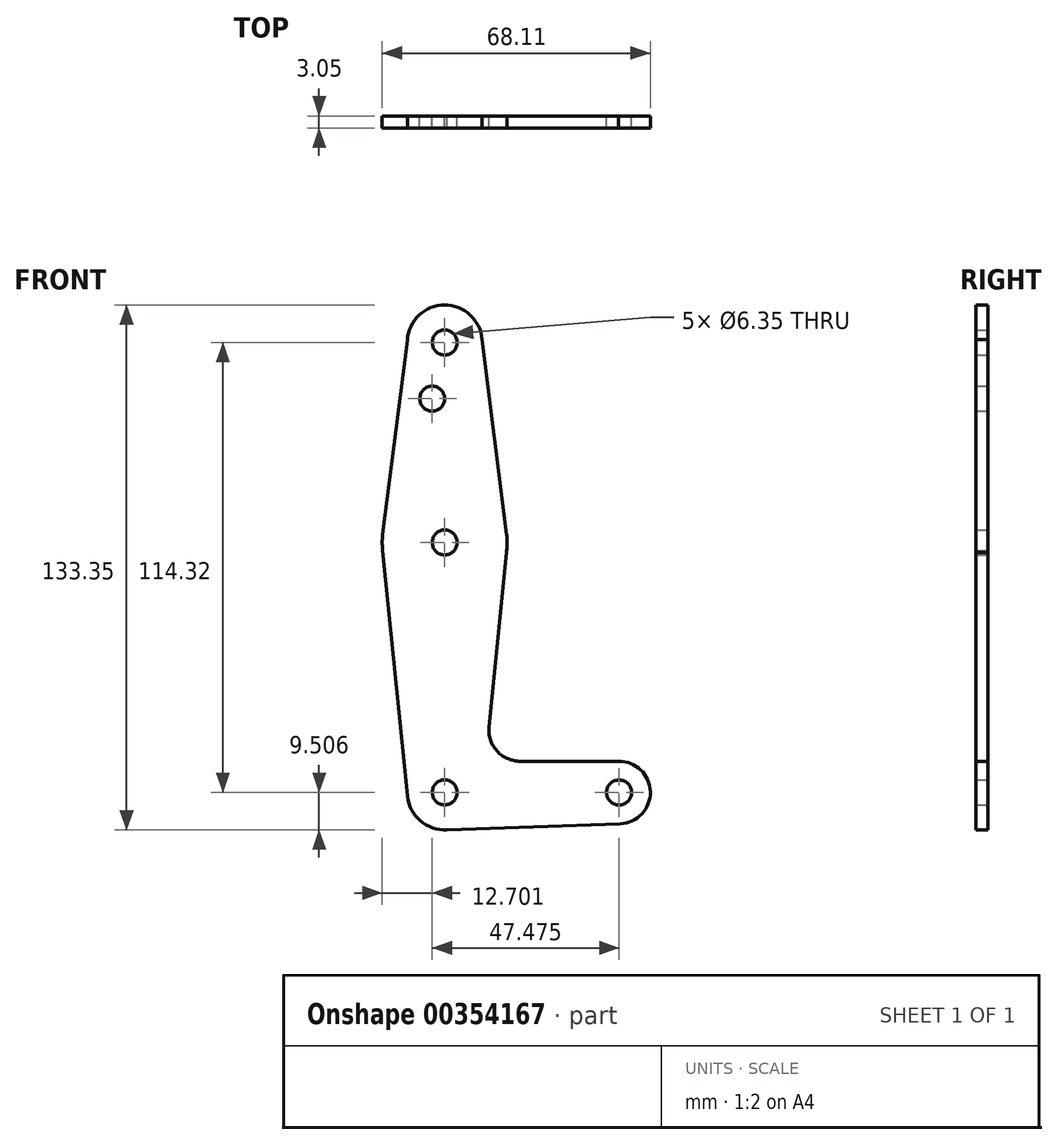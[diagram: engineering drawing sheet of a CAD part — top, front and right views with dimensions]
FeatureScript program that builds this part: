
annotation { "Feature Type Name" : "Feature", "Feature Type Description" : "" }
export const myFeature = defineFeature(function(context is Context, id is Id, definition is map)
    precondition{}
    {
        {
            var Q0;
            Q0=qCreatedBy(makeId("Front.planeOp"),FACE);
            var sketch = newSketch(context, id + "F0", { "sketchPlane" : qUnion([Q0])});
            skLineSegment(sketch, "E0", {"start": v(-36.37, 29.3) * mm, "end": v(-36.37, -85) * mm, "construction": true});
            skCircle(sketch, "E1", {"center": v(-36.37, 29.3) * mm, "radius": 9.53 * mm});
            skCircle(sketch, "E2", {"center": v(-36.37, -85) * mm, "radius": 9.53 * mm});
            skLineSegment(sketch, "E3", {"start": v(-36.52, -85.01) * mm, "end": v(7.93, -85.01) * mm, "construction": true});
            skCircle(sketch, "E4", {"center": v(7.93, -85.01) * mm, "radius": 7.94 * mm});
            skCircle(sketch, "E5", {"center": v(-36.37, -21.5) * mm, "radius": 15.88 * mm});
            skLineSegment(sketch, "E6", {"start": v(-26.88, 30.02) * mm, "end": v(-20.62, -19.5) * mm});
            skLineSegment(sketch, "E7", {"start": v(-45.74, 31.06) * mm, "end": v(-52.12, -19.5) * mm});
            skLineSegment(sketch, "E8", {"start": v(-52.12, -23.5) * mm, "end": v(-45.85, -85.95) * mm});
            skLineSegment(sketch, "E9", {"start": v(-20.7, -24.06) * mm, "end": v(-25.14, -68.34) * mm});
            skLineSegment(sketch, "E10", {"start": v(-36.26, -94.52) * mm, "end": v(8.2, -92.95) * mm});
            skLineSegment(sketch, "E11", {"start": v(7.8, -77.08) * mm, "end": v(-17.22, -77.08) * mm});
            skArc(sketch, "E12.filletArc", {"start": v(-25.14, -68.34) * mm, "mid": v(-23.12, -74.46) * mm, "end": v(-17.22, -77.08) * mm});
            skCircle(sketch, "E13", {"center": v(-36.37, 29.3) * mm, "radius": 3.18 * mm});
            skCircle(sketch, "E14", {"center": v(-36.37, -21.5) * mm, "radius": 3.18 * mm});
            skCircle(sketch, "E15", {"center": v(-36.37, -85) * mm, "radius": 3.18 * mm});
            skCircle(sketch, "E16", {"center": v(7.93, -85.01) * mm, "radius": 3.18 * mm});
            skCircle(sketch, "E17", {"center": v(-39.55, 15.03) * mm, "radius": 3.18 * mm});
            skSolve(sketch);
        }
        {
            var Q0;
            Q0 = qSketchRegion(id + "F0", true);
            extrude(context, id + "F1", {"entities" : qUnion([Q0]), "depth" : 3.05 * mm});
        }
    });
